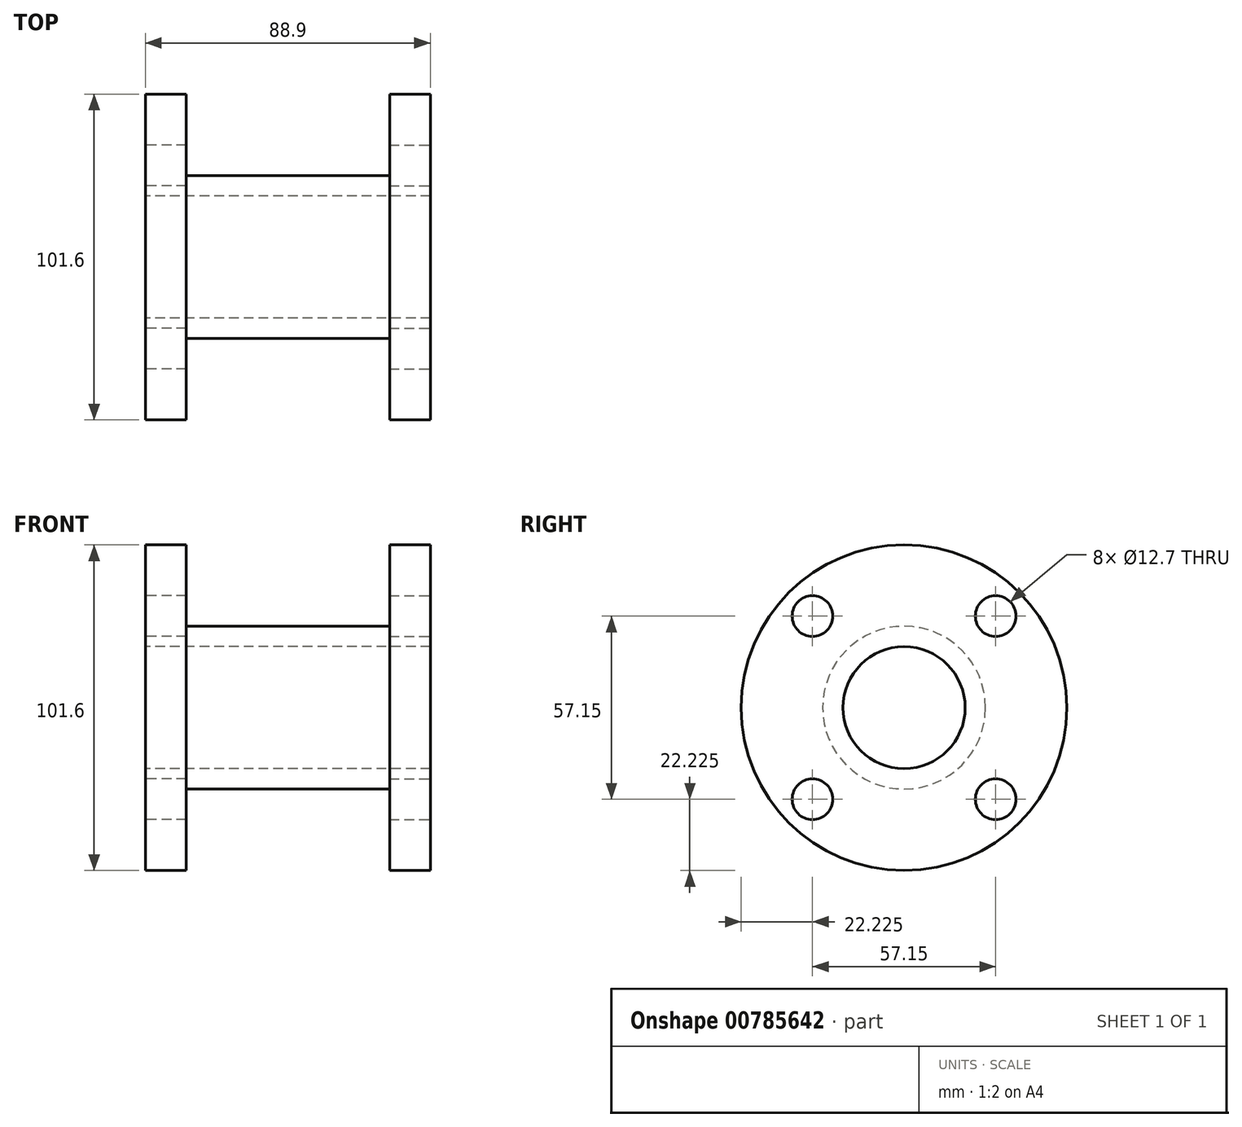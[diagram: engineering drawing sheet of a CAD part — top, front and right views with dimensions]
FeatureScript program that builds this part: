
annotation { "Feature Type Name" : "Feature", "Feature Type Description" : "" }
export const myFeature = defineFeature(function(context is Context, id is Id, definition is map)
    precondition{}
    {
        {
            var Q0;
            Q0=qCreatedBy(makeId("Right.planeOp"),FACE);
            var sketch = newSketch(context, id + "F0", { "sketchPlane" : qUnion([Q0])});
            skCircle(sketch, "E0", {"center": v(0, 0) * mm, "radius": 50.8 * mm});
            skCircle(sketch, "E1", {"center": v(0, 0) * mm, "radius": 19.05 * mm});
            skCircle(sketch, "E2", {"center": v(-28.58, 28.58) * mm, "radius": 6.35 * mm});
            skCircle(sketch, "E3", {"center": v(28.58, 28.58) * mm, "radius": 6.35 * mm});
            skCircle(sketch, "E4", {"center": v(28.58, -28.57) * mm, "radius": 6.35 * mm});
            skCircle(sketch, "E5", {"center": v(-28.57, -28.58) * mm, "radius": 6.35 * mm});
            skLineSegment(sketch, "E6", {"start": v(0, 50.8) * mm, "end": v(0, -50.8) * mm, "construction": true});
            skLineSegment(sketch, "E7", {"start": v(-50.8, 0) * mm, "end": v(50.8, 0) * mm, "construction": true});
            skLineSegment(sketch, "E8", {"start": v(-28.58, 28.58) * mm, "end": v(-28.57, 0) * mm, "construction": true});
            skLineSegment(sketch, "E9", {"start": v(-28.58, 0) * mm, "end": v(-28.57, -28.58) * mm, "construction": true});
            skLineSegment(sketch, "E10", {"start": v(28.58, -28.58) * mm, "end": v(0, -28.58) * mm, "construction": true});
            skCircle(sketch, "E11", {"center": v(0, 0) * mm, "radius": 25.4 * mm});
            skSolve(sketch);
        }
        {
            var Q0;
            Q0=qSketchRegion(id+"F0",true);
            extrude(context, id + "F1", {"entities" : qUnion([Q0]), "depth" : 12.7 * mm, "offsetDistance" : 25.4 * mm});
        }
        {
            var Q0;
            Q0=makeQuery(id+"F0.imprint","IMPRINT",FACE,{"disambiguationData":[TD([[makeQuery(id+"F0.imprint","IMPRINT",EDGE,{"derivedFrom":sQuery(id+"F0.wireOp",EDGE,"E1")}),-1.0]])]});
            extrude(context, id + "F2", {"entities" : qUnion([Q0]), "operationType" : NewBodyOperationType.ADD, "depth" : 88.9 * mm, "offsetDistance" : 25.4 * mm});
        }
        {
            var Q0;
            Q0=makeQuery(id+"F2.opExtrude","CAP_FACE",FACE,{"disambiguationData":[OSD([sQuery(id+"F0.wireOp",EDGE,"E1"),sQuery(id+"F0.wireOp",EDGE,"E11")])],"isStart":false});
            var sketch = newSketch(context, id + "F3", { "sketchPlane" : qUnion([Q0])});
            skCircle(sketch, "E12", {"center": v(0, 0) * mm, "radius": 50.8 * mm});
            skCircle(sketch, "E13", {"center": v(0, 0) * mm, "radius": 19.05 * mm});
            skCircle(sketch, "E14", {"center": v(-28.57, 28.58) * mm, "radius": 6.35 * mm});
            skCircle(sketch, "E15", {"center": v(28.58, 28.58) * mm, "radius": 6.35 * mm});
            skCircle(sketch, "E16", {"center": v(28.58, -28.58) * mm, "radius": 6.35 * mm});
            skCircle(sketch, "E17", {"center": v(-28.57, -28.58) * mm, "radius": 6.35 * mm});
            skLineSegment(sketch, "E18", {"start": v(0, 50.8) * mm, "end": v(0, -50.8) * mm, "construction": true});
            skLineSegment(sketch, "E19", {"start": v(-50.8, 0) * mm, "end": v(50.8, 0) * mm, "construction": true});
            skLineSegment(sketch, "E20", {"start": v(-28.57, 28.58) * mm, "end": v(-28.57, 0) * mm, "construction": true});
            skLineSegment(sketch, "E21", {"start": v(-28.57, 0) * mm, "end": v(-28.57, -28.58) * mm, "construction": true});
            skLineSegment(sketch, "E22", {"start": v(28.58, -28.57) * mm, "end": v(0, -28.58) * mm, "construction": true});
            skCircle(sketch, "E23", {"center": v(0, 0) * mm, "radius": 25.4 * mm});
            skSolve(sketch);
        }
        {
            var Q0;
            Q0=qSketchRegion(id+"F3",true);
            extrude(context, id + "F4", {"entities" : qUnion([Q0]), "operationType" : NewBodyOperationType.ADD, "oppositeDirection" : true, "depth" : 12.7 * mm, "offsetDistance" : 25.4 * mm});
        }
    });
